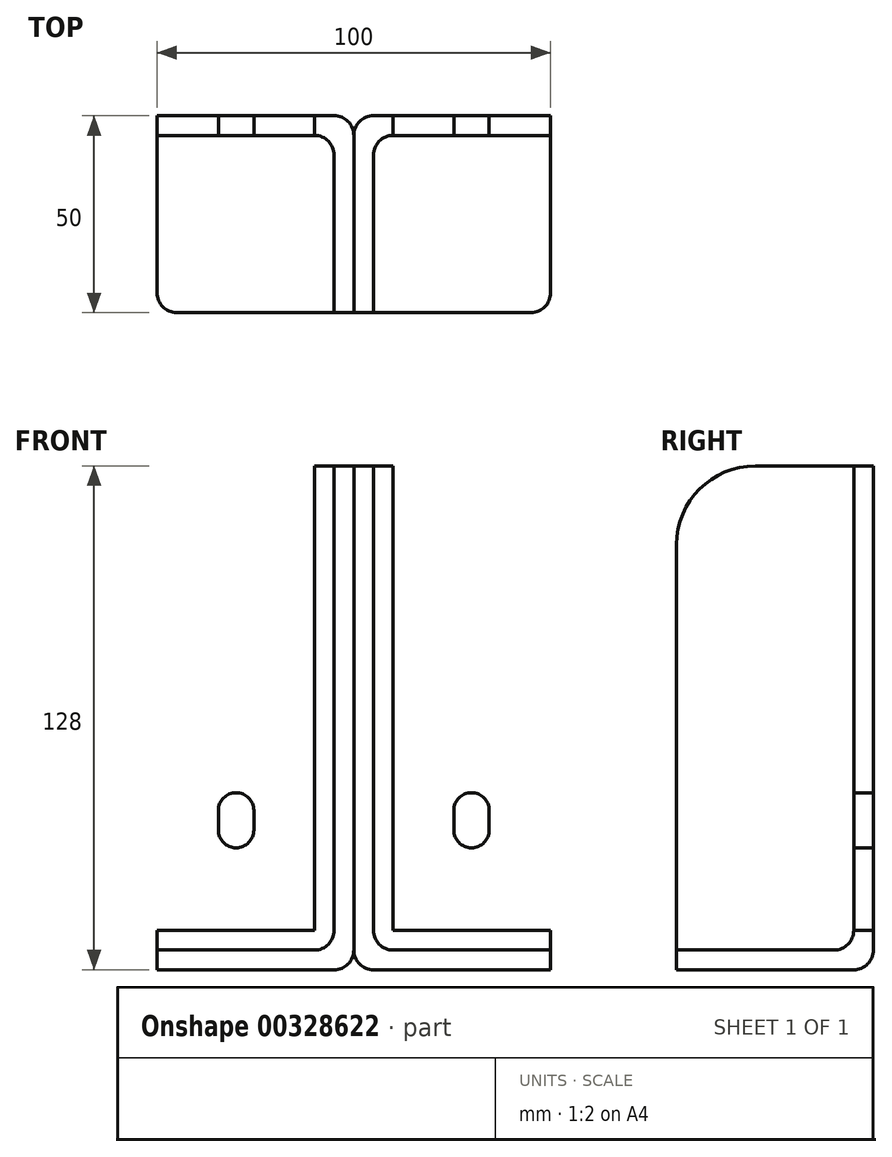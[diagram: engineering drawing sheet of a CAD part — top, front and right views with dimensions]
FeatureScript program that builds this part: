
annotation { "Feature Type Name" : "Feature", "Feature Type Description" : "" }
export const myFeature = defineFeature(function(context is Context, id is Id, definition is map)
    precondition{}
    {
        {
            var Q0;
            Q0=qCreatedBy(makeId("Top.planeOp"),FACE);
            var sketch = newSketch(context, id + "F0", { "sketchPlane" : qUnion([Q0])});
            skLineSegment(sketch, "E0.bottom", {"start": v(0, 0) * mm, "end": v(50, 0) * mm});
            skLineSegment(sketch, "E0.top", {"start": v(0, -50) * mm, "end": v(50, -50) * mm});
            skLineSegment(sketch, "E0.left", {"start": v(0, 0) * mm, "end": v(0, -50) * mm});
            skLineSegment(sketch, "E0.right", {"start": v(50, 0) * mm, "end": v(50, -50) * mm});
            skSolve(sketch);
        }
        {
            var Q0;
            Q0=makeQuery(id+"F0.imprint","IMPRINT",FACE,{"disambiguationData":[TD([[makeQuery(id+"F0.imprint","IMPRINT",EDGE,{"derivedFrom":sQuery(id+"F0.wireOp",EDGE,"E0.bottom")}),-1.0]])]});
            extrude(context, id + "F1", {"entities" : qUnion([Q0]), "depth" : 128 * mm});
        }
        {
            var Q0;
            Q0=makeQuery(id+"F1.opExtrude","CAP_FACE",FACE,{"disambiguationData":[OSD([sQuery(id+"F0.wireOp",EDGE,"E0.bottom"),sQuery(id+"F0.wireOp",EDGE,"E0.top"),sQuery(id+"F0.wireOp",EDGE,"E0.left"),sQuery(id+"F0.wireOp",EDGE,"E0.right")])],"isStart":false});
            var sketch = newSketch(context, id + "F2", { "sketchPlane" : qUnion([Q0])});
            skLineSegment(sketch, "E1.bottom", {"start": v(50, -50) * mm, "end": v(5, -50) * mm});
            skLineSegment(sketch, "E1.top", {"start": v(50, -5) * mm, "end": v(5, -5) * mm});
            skLineSegment(sketch, "E1.left", {"start": v(50, -50) * mm, "end": v(50, -5) * mm});
            skLineSegment(sketch, "E1.right", {"start": v(5, -50) * mm, "end": v(5, -5) * mm});
            skSolve(sketch);
        }
        {
            var Q0;
            Q0=makeQuery(id+"F2.imprint","IMPRINT",FACE,{"disambiguationData":[TD([[makeQuery(id+"F2.imprint","IMPRINT",EDGE,{"derivedFrom":sQuery(id+"F2.wireOp",EDGE,"E1.bottom")}),1.0]])]});
            extrude(context, id + "F3", {"entities" : qUnion([Q0]), "operationType" : NewBodyOperationType.REMOVE, "oppositeDirection" : true, "depth" : 123 * mm});
        }
        {
            var Q0;
            Q0=makeQuery(id+"F3.boolean.opBoolean","COPY",EDGE,{"derivedFrom":makeQuery(id+"F3.opExtrude","SWEPT_EDGE",EDGE,{"disambiguationData":[OSD([sQuery(id+"F2.wireOp",EDGE,"E1.top"),sQuery(id+"F2.wireOp",EDGE,"E1.right")])]})});
            var Q1;
            Q1=makeQuery(id+"F1.opExtrude","SWEPT_EDGE",EDGE,{"disambiguationData":[OSD([sQuery(id+"F0.wireOp",EDGE,"E0.bottom"),sQuery(id+"F0.wireOp",EDGE,"E0.left")])]});
            var Q2;
            Q2=makeQuery(id+"F1.opExtrude","CAP_EDGE",EDGE,{"disambiguationData":[OSD([sQuery(id+"F0.wireOp",EDGE,"E0.bottom")])],"isStart":true});
            var Q3;
            Q3=makeQuery(id+"F1.opExtrude","CAP_EDGE",EDGE,{"disambiguationData":[OSD([sQuery(id+"F0.wireOp",EDGE,"E0.left")])],"isStart":true});
            var Q4;
            Q4=makeQuery(id+"F3.boolean.opBoolean","COPY",EDGE,{"derivedFrom":makeQuery(id+"F3.opExtrude","CAP_EDGE",EDGE,{"disambiguationData":[OSD([sQuery(id+"F2.wireOp",EDGE,"E1.right")])],"isStart":false})});
            var Q5;
            Q5=makeQuery(id+"F3.boolean.opBoolean","COPY",EDGE,{"derivedFrom":makeQuery(id+"F3.opExtrude","CAP_EDGE",EDGE,{"disambiguationData":[OSD([sQuery(id+"F2.wireOp",EDGE,"E1.top")])],"isStart":false})});
            var Q6;
            Q6=makeQuery(id+"F1.opExtrude","CAP_EDGE",EDGE,{"disambiguationData":[OSD([sQuery(id+"F0.wireOp",EDGE,"E0.right")])],"isStart":false});
            var Q7;
            Q7=makeQuery(id+"F1.opExtrude","SWEPT_EDGE",EDGE,{"disambiguationData":[OSD([sQuery(id+"F0.wireOp",EDGE,"E0.top"),sQuery(id+"F0.wireOp",EDGE,"E0.right")])]});
            fillet(context, id + "F4", {"entities" : qUnion([Q0, Q1, Q2, Q3, Q4, Q5, Q6, Q7]), "radius" : 5 * mm, "tangentPropagation" : true, "allowEdgeOverflow" : false});
        }
        {
            var Q0;
            Q0=makeQuery(id+"F1.opExtrude","CAP_EDGE",EDGE,{"disambiguationData":[OSD([sQuery(id+"F0.wireOp",EDGE,"E0.top")])],"isStart":false});
            fillet(context, id + "F5", {"entities" : qUnion([Q0]), "radius" : 20 * mm, "tangentPropagation" : true, "allowEdgeOverflow" : false});
        }
        {
            var Q0;
            Q0=makeQuery(id+"F3.boolean.opBoolean","COPY",FACE,{"derivedFrom":makeQuery(id+"F3.opExtrude","SWEPT_FACE",FACE,{"disambiguationData":[OSD([sQuery(id+"F2.wireOp",EDGE,"E1.top")])]})});
            var sketch = newSketch(context, id + "F6", { "sketchPlane" : qUnion([Q0])});
            skLineSegment(sketch, "E2.bottom", {"start": v(29.9, 110) * mm, "end": v(29.9, 110) * mm});
            skLineSegment(sketch, "E2.top", {"start": v(29.9, 96) * mm, "end": v(29.9, 96) * mm});
            skLineSegment(sketch, "E2.left", {"start": v(25.4, 105.5) * mm, "end": v(25.4, 100.5) * mm});
            skLineSegment(sketch, "E2.right", {"start": v(34.4, 105.5) * mm, "end": v(34.4, 100.5) * mm});
            skPoint(sketch, "E3.visualSharp", {"position": v(25.4, 110) * mm});
            skArc(sketch, "E3.filletArc", {"start": v(29.9, 110) * mm, "mid": v(26.72, 108.68) * mm, "end": v(25.4, 105.5) * mm});
            skPoint(sketch, "E4.visualSharp", {"position": v(34.4, 110) * mm});
            skArc(sketch, "E4.filletArc", {"start": v(34.4, 105.5) * mm, "mid": v(33.08, 108.68) * mm, "end": v(29.9, 110) * mm});
            skPoint(sketch, "E5.visualSharp", {"position": v(25.4, 96) * mm});
            skArc(sketch, "E5.filletArc", {"start": v(25.4, 100.5) * mm, "mid": v(26.72, 97.32) * mm, "end": v(29.9, 96) * mm});
            skPoint(sketch, "E6.visualSharp", {"position": v(34.4, 96) * mm});
            skArc(sketch, "E6.filletArc", {"start": v(29.9, 96) * mm, "mid": v(33.08, 97.32) * mm, "end": v(34.4, 100.5) * mm});
            skArc(sketch, "E7.MirrorCS", {"start": v(29.9, 45) * mm, "mid": v(33.08, 43.68) * mm, "end": v(34.4, 40.5) * mm});
            skLineSegment(sketch, "E8.MirrorCS", {"start": v(34.4, 35.5) * mm, "end": v(34.4, 40.5) * mm});
            skArc(sketch, "E9.MirrorCS", {"start": v(34.4, 35.5) * mm, "mid": v(33.08, 32.32) * mm, "end": v(29.9, 31) * mm});
            skArc(sketch, "E10.MirrorCS", {"start": v(29.9, 31) * mm, "mid": v(26.72, 32.32) * mm, "end": v(25.4, 35.5) * mm});
            skLineSegment(sketch, "E11.MirrorCS", {"start": v(25.4, 35.5) * mm, "end": v(25.4, 40.5) * mm});
            skArc(sketch, "E12.MirrorCS", {"start": v(25.4, 40.5) * mm, "mid": v(26.72, 43.68) * mm, "end": v(29.9, 45) * mm});
            skSolve(sketch);
        }
        {
            var Q0;
            Q0=makeQuery(id+"F6.imprint","IMPRINT",FACE,{"disambiguationData":[TD([[makeQuery(id+"F6.imprint","IMPRINT",EDGE,{"derivedFrom":sQuery(id+"F6.wireOp",EDGE,"E2.left")}),1.0]])]});
            var Q1;
            Q1=makeQuery(id+"F6.imprint","IMPRINT",FACE,{"disambiguationData":[TD([[makeQuery(id+"F6.imprint","IMPRINT",EDGE,{"derivedFrom":sQuery(id+"F6.wireOp",EDGE,"E7.MirrorCS")}),-1.0]])]});
            extrude(context, id + "F7", {"entities" : qUnion([Q0, Q1]), "operationType" : NewBodyOperationType.REMOVE, "endBound" : BoundingType.THROUGH_ALL, "oppositeDirection" : true, "depth" : 25 * mm});
        }
        {
            var Q0;
            Q0=makeQuery(id+"F1.opExtrude","SWEPT_BODY",BODY,{"disambiguationData":[OSD([sQuery(id+"F0.wireOp",EDGE,"E0.bottom"),sQuery(id+"F0.wireOp",EDGE,"E0.top"),sQuery(id+"F0.wireOp",EDGE,"E0.left"),sQuery(id+"F0.wireOp",EDGE,"E0.right")])]});
            var Q1;
            Q1=qCreatedBy(makeId("Right.planeOp"),FACE);
            mirror(context, id + "F8", {"entities" : qUnion([Q0]), "mirrorPlane" : qUnion([Q1])});
        }
    });
